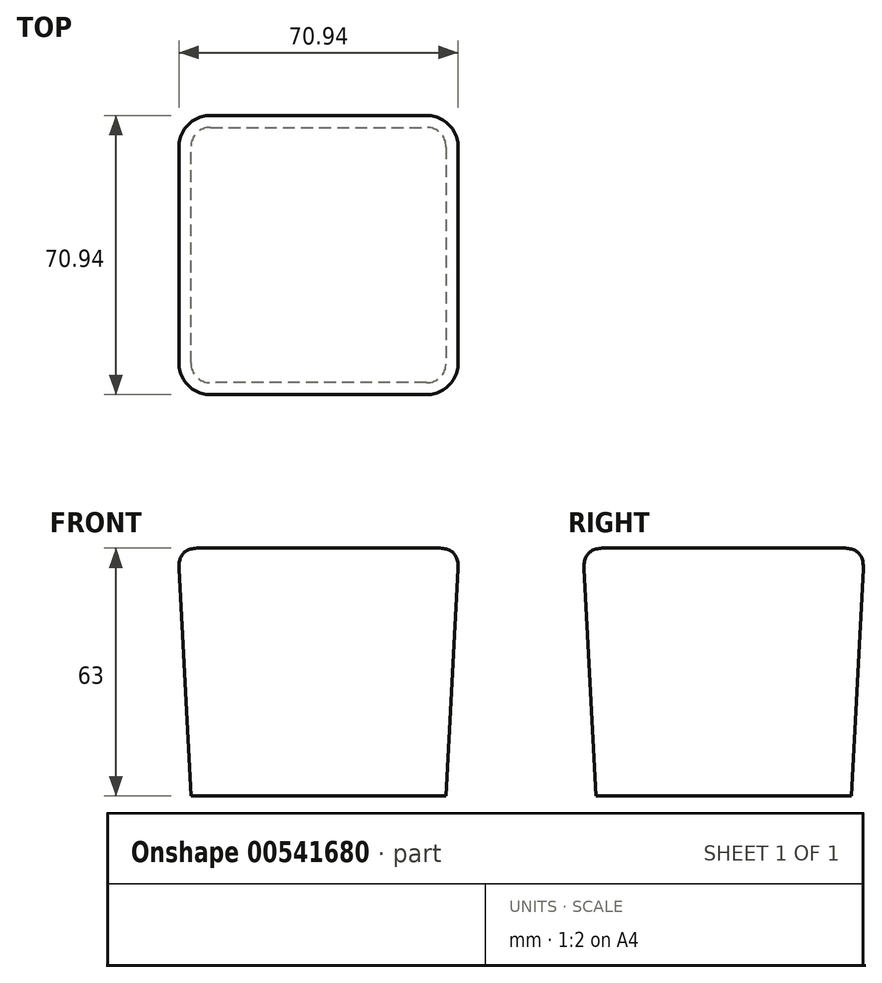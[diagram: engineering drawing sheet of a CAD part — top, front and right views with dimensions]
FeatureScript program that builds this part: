
annotation { "Feature Type Name" : "Feature", "Feature Type Description" : "" }
export const myFeature = defineFeature(function(context is Context, id is Id, definition is map)
    precondition{}
    {
        {
            var Q0;
            Q0=qCreatedBy(makeId("Top.planeOp"),FACE);
            var sketch = newSketch(context, id + "F0", { "sketchPlane" : qUnion([Q0])});
            skLineSegment(sketch, "E0.bottom", {"start": v(-20.86, 3.55) * mm, "end": v(-75.72, 3.55) * mm});
            skLineSegment(sketch, "E0.top", {"start": v(-20.86, 68.4) * mm, "end": v(-75.72, 68.4) * mm});
            skLineSegment(sketch, "E0.left", {"start": v(-15.86, 8.55) * mm, "end": v(-15.86, 63.4) * mm});
            skLineSegment(sketch, "E0.right", {"start": v(-80.72, 8.55) * mm, "end": v(-80.72, 63.4) * mm});
            skPoint(sketch, "E0.middle", {"position": v(-48.3, 35.98) * mm});
            skPoint(sketch, "E1.visualSharp", {"position": v(-80.72, 68.4) * mm});
            skArc(sketch, "E1.filletArc", {"start": v(-75.72, 68.4) * mm, "mid": v(-79.26, 66.94) * mm, "end": v(-80.72, 63.4) * mm});
            skPoint(sketch, "E2.visualSharp", {"position": v(-15.86, 68.4) * mm});
            skArc(sketch, "E2.filletArc", {"start": v(-15.86, 63.4) * mm, "mid": v(-17.33, 66.94) * mm, "end": v(-20.86, 68.4) * mm});
            skPoint(sketch, "E3.visualSharp", {"position": v(-15.86, 3.55) * mm});
            skArc(sketch, "E3.filletArc", {"start": v(-20.86, 3.55) * mm, "mid": v(-17.33, 5.01) * mm, "end": v(-15.86, 8.55) * mm});
            skPoint(sketch, "E4.visualSharp", {"position": v(-80.72, 3.55) * mm});
            skArc(sketch, "E4.filletArc", {"start": v(-80.72, 8.55) * mm, "mid": v(-79.26, 5.01) * mm, "end": v(-75.72, 3.55) * mm});
            skSolve(sketch);
        }
        {
            var Q0;
            Q0=makeQuery(id+"F0.imprint","IMPRINT",FACE,{"disambiguationData":[TD([[makeQuery(id+"F0.imprint","IMPRINT",EDGE,{"derivedFrom":sQuery(id+"F0.wireOp",EDGE,"E0.bottom")}),-1.0]])]});
            extrude(context, id + "F1", {"entities" : qUnion([Q0]), "depth" : 63 * mm, "offsetDistance" : 25 * mm, "hasDraft" : true, "draftAngle" : 3 * degree});
        }
        {
            var Q0;
            Q0=makeQuery(id+"F1.opExtrude","CAP_EDGE",EDGE,{"disambiguationData":[OSD([sQuery(id+"F0.wireOp",EDGE,"E0.bottom")])],"isStart":false});
            var Q1;
            Q1=makeQuery(id+"F1.opExtrude","CAP_FACE",FACE,{"disambiguationData":[OSD([sQuery(id+"F0.wireOp",EDGE,"E0.bottom"),sQuery(id+"F0.wireOp",EDGE,"E0.top"),sQuery(id+"F0.wireOp",EDGE,"E0.left"),sQuery(id+"F0.wireOp",EDGE,"E0.right"),sQuery(id+"F0.wireOp",EDGE,"E1.filletArc"),sQuery(id+"F0.wireOp",EDGE,"E2.filletArc"),sQuery(id+"F0.wireOp",EDGE,"E3.filletArc"),sQuery(id+"F0.wireOp",EDGE,"E4.filletArc")])],"isStart":false});
            fillet(context, id + "F2", {"entities" : qUnion([Q0, Q1]), "radius" : 5 * mm, "tangentPropagation" : true, "rho" : 0.5, "crossSection" : FilletCrossSection.CONIC, "allowEdgeOverflow" : false});
        }
    });
